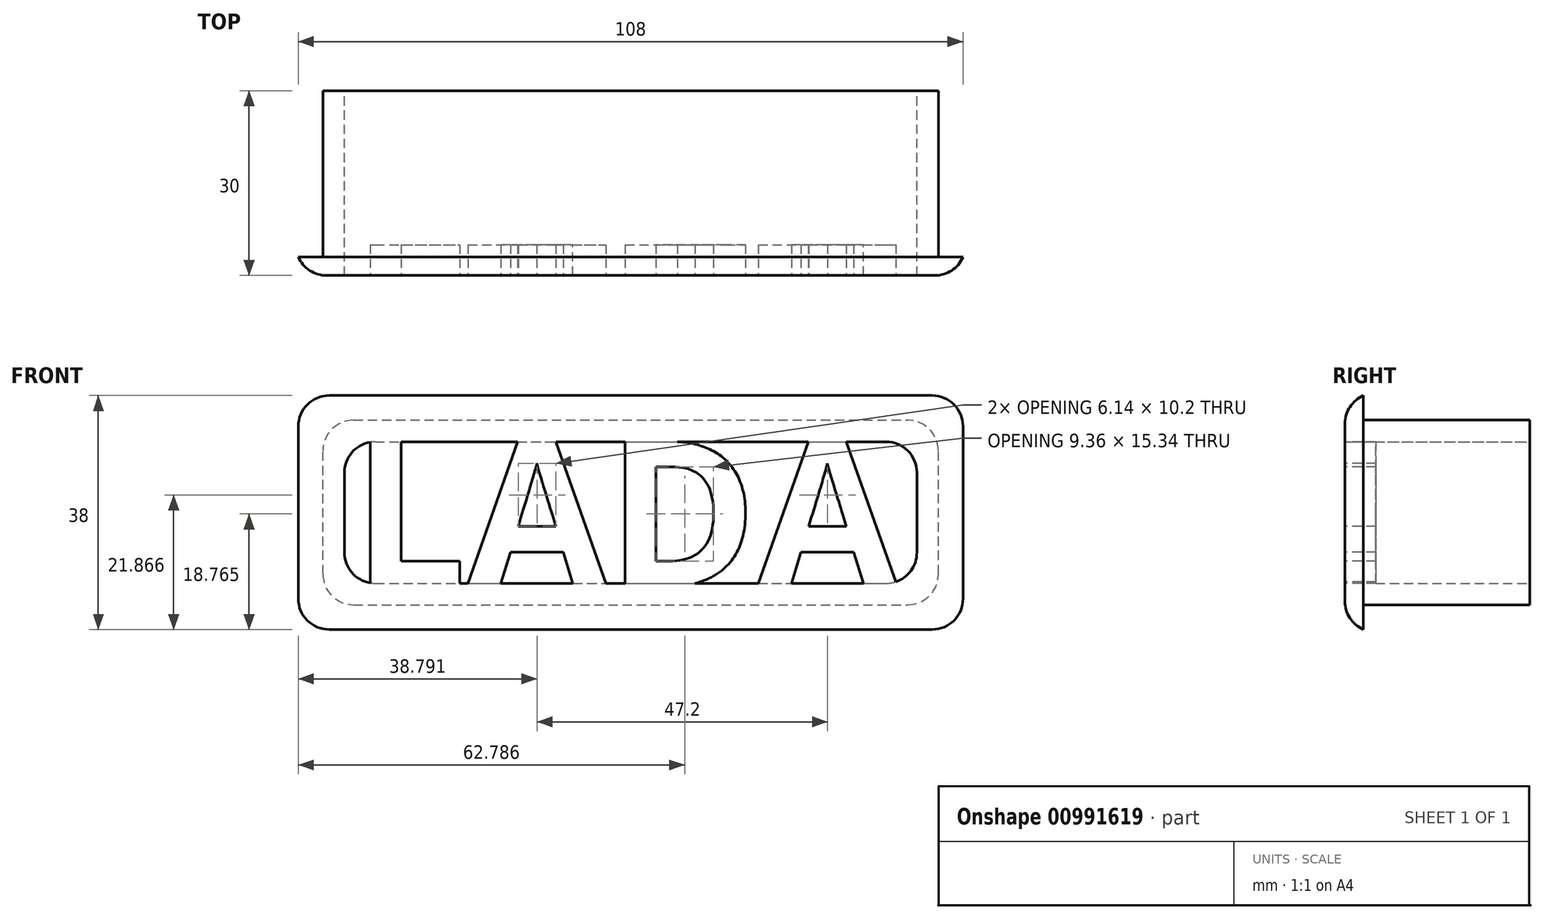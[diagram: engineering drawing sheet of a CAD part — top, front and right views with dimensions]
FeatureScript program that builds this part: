
annotation { "Feature Type Name" : "Feature", "Feature Type Description" : "" }
export const myFeature = defineFeature(function(context is Context, id is Id, definition is map)
    precondition{}
    {
        {
            var Q0;
            Q0=qCreatedBy(makeId("Front.planeOp"),FACE);
            var sketch = newSketch(context, id + "F0", { "sketchPlane" : qUnion([Q0])});
            skLineSegment(sketch, "E0.bottom", {"start": v(0, 0) * mm, "end": v(100, 0) * mm});
            skLineSegment(sketch, "E0.top", {"start": v(0, 30) * mm, "end": v(100, 30) * mm});
            skLineSegment(sketch, "E0.left", {"start": v(0, 0) * mm, "end": v(0, 30) * mm});
            skLineSegment(sketch, "E0.right", {"start": v(100, 0) * mm, "end": v(100, 30) * mm});
            skLineSegment(sketch, "E1.bottom", {"start": v(3.5, 3.5) * mm, "end": v(96.5, 3.5) * mm});
            skLineSegment(sketch, "E1.top", {"start": v(3.5, 26.5) * mm, "end": v(96.5, 26.5) * mm});
            skLineSegment(sketch, "E1.left", {"start": v(3.5, 3.5) * mm, "end": v(3.5, 26.5) * mm});
            skLineSegment(sketch, "E1.right", {"start": v(96.5, 3.5) * mm, "end": v(96.5, 26.5) * mm});
            skLineSegment(sketch, "E2", {"start": v(0, 15) * mm, "end": v(100, 15) * mm, "construction": true});
            skPoint(sketch, "E2.endSnap0", {"position": v(96.5, 15) * mm});
            skLineSegment(sketch, "E3", {"start": v(50, 30) * mm, "end": v(50, 0) * mm, "construction": true});
            skSolve(sketch);
        }
        {
            var Q0;
            Q0=makeQuery(id+"F0.imprint","IMPRINT",FACE,{"disambiguationData":[TD([[makeQuery(id+"F0.imprint","IMPRINT",EDGE,{"derivedFrom":sQuery(id+"F0.wireOp",EDGE,"E0.bottom")}),1.0]])]});
            extrude(context, id + "F1", {"entities" : qUnion([Q0]), "depth" : 30 * mm, "offsetDistance" : 25 * mm});
        }
        {
            var Q0;
            Q0=makeQuery(id+"F1.opExtrude","CAP_FACE",FACE,{"disambiguationData":[OSD([sQuery(id+"F0.wireOp",EDGE,"E0.bottom"),sQuery(id+"F0.wireOp",EDGE,"E0.top"),sQuery(id+"F0.wireOp",EDGE,"E0.left"),sQuery(id+"F0.wireOp",EDGE,"E0.right"),sQuery(id+"F0.wireOp",EDGE,"E1.bottom"),sQuery(id+"F0.wireOp",EDGE,"E1.top"),sQuery(id+"F0.wireOp",EDGE,"E1.left"),sQuery(id+"F0.wireOp",EDGE,"E1.right")])],"isStart":false});
            var sketch = newSketch(context, id + "F2", { "sketchPlane" : qUnion([Q0])});
            skLineSegment(sketch, "E4.bottom", {"start": v(1, 34) * mm, "end": v(99, 34) * mm});
            skLineSegment(sketch, "E4.top", {"start": v(1, -4) * mm, "end": v(99, -4) * mm});
            skLineSegment(sketch, "E4.left", {"start": v(-4, 29) * mm, "end": v(-4, 1) * mm});
            skLineSegment(sketch, "E4.right", {"start": v(104, 29) * mm, "end": v(104, 1) * mm});
            skPoint(sketch, "E5.visualSharp", {"position": v(-4, 34) * mm});
            skArc(sketch, "E5.filletArc", {"start": v(1, 34) * mm, "mid": v(-2.54, 32.54) * mm, "end": v(-4, 29) * mm});
            skPoint(sketch, "E6.visualSharp", {"position": v(104, 34) * mm});
            skArc(sketch, "E6.filletArc", {"start": v(104, 29) * mm, "mid": v(102.54, 32.54) * mm, "end": v(99, 34) * mm});
            skPoint(sketch, "E7.visualSharp", {"position": v(104, -4) * mm});
            skArc(sketch, "E7.filletArc", {"start": v(99, -4) * mm, "mid": v(102.54, -2.54) * mm, "end": v(104, 1) * mm});
            skPoint(sketch, "E8.visualSharp", {"position": v(-4, -4) * mm});
            skArc(sketch, "E8.filletArc", {"start": v(-4, 1) * mm, "mid": v(-2.54, -2.54) * mm, "end": v(1, -4) * mm});
            skSolve(sketch);
        }
        {
            var Q0;
            Q0=makeQuery(id+"F2.imprint","IMPRINT",FACE,{"disambiguationData":[TD([[makeQuery(id+"F2.imprint","IMPRINT",EDGE,{"derivedFrom":sQuery(id+"F2.wireOp",EDGE,"E4.bottom")}),-1.0]])]});
            extrude(context, id + "F3", {"entities" : qUnion([Q0]), "operationType" : NewBodyOperationType.ADD, "oppositeDirection" : true, "depth" : 3 * mm, "offsetDistance" : 25 * mm});
        }
        {
            var Q0;
            Q0=makeQuery(id+"F3.opExtrude","CAP_EDGE",EDGE,{"disambiguationData":[OSD([sQuery(id+"F2.wireOp",EDGE,"E6.filletArc")])],"isStart":true});
            fillet(context, id + "F4", {"entities" : qUnion([Q0]), "radius" : 5 * mm, "tangentPropagation" : true, "allowEdgeOverflow" : false});
        }
        {
            var Q0;
            Q0=makeQuery(id+"F1.opExtrude","SWEPT_EDGE",EDGE,{"disambiguationData":[OSD([sQuery(id+"F0.wireOp",EDGE,"E1.top"),sQuery(id+"F0.wireOp",EDGE,"E1.right")])]});
            var Q1;
            Q1=makeQuery(id+"F1.opExtrude","SWEPT_EDGE",EDGE,{"disambiguationData":[OSD([sQuery(id+"F0.wireOp",EDGE,"E1.bottom"),sQuery(id+"F0.wireOp",EDGE,"E1.right")])]});
            var Q2;
            Q2=makeQuery(id+"F1.opExtrude","SWEPT_EDGE",EDGE,{"disambiguationData":[OSD([sQuery(id+"F0.wireOp",EDGE,"E1.top"),sQuery(id+"F0.wireOp",EDGE,"E1.left")])]});
            var Q3;
            Q3=makeQuery(id+"F1.opExtrude","SWEPT_EDGE",EDGE,{"disambiguationData":[OSD([sQuery(id+"F0.wireOp",EDGE,"E1.bottom"),sQuery(id+"F0.wireOp",EDGE,"E1.left")])]});
            var Q4;
            Q4=makeQuery(id+"F1.opExtrude","SWEPT_EDGE",EDGE,{"disambiguationData":[OSD([sQuery(id+"F0.wireOp",EDGE,"E0.top"),sQuery(id+"F0.wireOp",EDGE,"E0.right")])]});
            var Q5;
            Q5=makeQuery(id+"F1.opExtrude","SWEPT_EDGE",EDGE,{"disambiguationData":[OSD([sQuery(id+"F0.wireOp",EDGE,"E0.top"),sQuery(id+"F0.wireOp",EDGE,"E0.left")])]});
            var Q6;
            Q6=makeQuery(id+"F1.opExtrude","SWEPT_EDGE",EDGE,{"disambiguationData":[OSD([sQuery(id+"F0.wireOp",EDGE,"E0.bottom"),sQuery(id+"F0.wireOp",EDGE,"E0.left")])]});
            var Q7;
            Q7=makeQuery(id+"F1.opExtrude","SWEPT_EDGE",EDGE,{"disambiguationData":[OSD([sQuery(id+"F0.wireOp",EDGE,"E0.bottom"),sQuery(id+"F0.wireOp",EDGE,"E0.right")])]});
            fillet(context, id + "F5", {"entities" : qUnion([Q0, Q1, Q2, Q3, Q4, Q5, Q6, Q7]), "radius" : 5 * mm, "tangentPropagation" : true, "allowEdgeOverflow" : false});
        }
        {
            var Q0;
            Q0=qCreatedBy(makeId("Front.planeOp"),FACE);
            var sketch = newSketch(context, id + "F6", { "sketchPlane" : qUnion([Q0])});
            skFitSpline(sketch, "E9", {"points": [v(-64.61, 66.28) * mm, v(-47.68, 57.17) * mm, v(-34.75, 47.89) * mm, v(-23.1, 43.7) * mm, v(-14.9, 33.87) * mm, v(-19.1, 24.22) * mm, v(-39.3, 28.4) * mm, v(-52.96, 38.42) * mm, v(-69.35, 37.87) * mm, v(-90.29, 48.07) * mm, v(-89.38, 58.45) * mm, v(-64.61, 66.28) * mm]});
            skSolve(sketch);
        }
        {
            var Q0;
            Q0=makeQuery(id+"F6.imprint","IMPRINT",FACE,{"disambiguationData":[TD([[makeQuery(id+"F6.imprint","IMPRINT",EDGE,{"derivedFrom":sQuery(id+"F6.wireOp",EDGE,"E9")}),-1.0]])]});
            extrude(context, id + "F7", {"entities" : qUnion([Q0]), "depth" : 25 * mm, "offsetDistance" : 25 * mm});
        }
        {
            var Q0;
            Q0=makeQuery(id+"F7.opExtrude","CAP_FACE",FACE,{"disambiguationData":[OSD([sQuery(id+"F6.wireOp",EDGE,"E9")])],"isStart":false});
            shell(context, id + "F8", {"entities" : qUnion([Q0]), "thickness" : 4 * mm});
        }
        {
            var Q0;
            Q0=makeQuery(id+"F7.opExtrude","SWEPT_BODY",BODY,{"disambiguationData":[OSD([sQuery(id+"F6.wireOp",EDGE,"E9")])]});
            deleteBodies(context, id + "F9", {"entities" : qUnion([Q0])});
        }
        {
            var Q0;
            {var subQ0=sQuery(id+"F0.wireOp",EDGE,"E0.right");var subQ1=sQuery(id+"F0.wireOp",EDGE,"E0.left");var subQ2=sQuery(id+"F0.wireOp",EDGE,"E0.top");var subQ3=sQuery(id+"F0.wireOp",EDGE,"E0.bottom");Q0=makeQuery(id+"F3.boolean.opBoolean","MERGE",FACE,{"derivedFrom":[makeQuery(id+"F1.opExtrude","CAP_FACE",FACE,{"disambiguationData":[OSD([subQ3,subQ2,subQ1,subQ0,sQuery(id+"F0.wireOp",EDGE,"E1.bottom"),sQuery(id+"F0.wireOp",EDGE,"E1.top"),sQuery(id+"F0.wireOp",EDGE,"E1.left"),sQuery(id+"F0.wireOp",EDGE,"E1.right")])],"isStart":false}),makeQuery(id+"F3.opExtrude","CAP_FACE",FACE,{"disambiguationData":[OSD([subQ3,subQ2,subQ1,subQ0,sQuery(id+"F2.wireOp",EDGE,"E4.bottom"),sQuery(id+"F2.wireOp",EDGE,"E4.top"),sQuery(id+"F2.wireOp",EDGE,"E4.left"),sQuery(id+"F2.wireOp",EDGE,"E4.right"),sQuery(id+"F2.wireOp",EDGE,"E5.filletArc"),sQuery(id+"F2.wireOp",EDGE,"E6.filletArc"),sQuery(id+"F2.wireOp",EDGE,"E7.filletArc"),sQuery(id+"F2.wireOp",EDGE,"E8.filletArc")])],"isStart":true})]});}
            var sketch = newSketch(context, id + "F10", { "sketchPlane" : qUnion([Q0])});
            skText(sketch, "E10", { "text": "LADA", "fontName": "OpenSans-Bold.ttf"});
            const initialGuessF10  = {"E10": [0.00473, 0.00297, 1, 0, 0.02376]};
            skSetInitialGuess(sketch, initialGuessF10);
            skSolve(sketch);
        }
        {
            var Q0;
            {var subQ0=sQuery(id+"F10.wireOp",EDGE,"E10.sketch_text.stroke-1");Q0=makeQuery(id+"F10.imprint","IMPRINT",FACE,{"disambiguationData":[TD([[makeQuery(id+"F10.imprint","IMPRINT",EDGE,{"derivedFrom":subQ0}),-1.0]])]});}
            var Q1;
            Q1=makeQuery(id+"F10.imprint","IMPRINT",FACE,{"disambiguationData":[TD([[makeQuery(id+"F10.imprint","IMPRINT",EDGE,{"derivedFrom":sQuery(id+"F10.wireOp",EDGE,"E10.sketch_text.stroke-6")}),-1.0]])]});
            var Q2;
            Q2=makeQuery(id+"F10.imprint","IMPRINT",FACE,{"disambiguationData":[TD([[makeQuery(id+"F10.imprint","IMPRINT",EDGE,{"derivedFrom":sQuery(id+"F10.wireOp",EDGE,"E10.sketch_text.stroke-18")}),-1.0]])]});
            var Q3;
            Q3=makeQuery(id+"F10.imprint","IMPRINT",FACE,{"disambiguationData":[TD([[makeQuery(id+"F10.imprint","IMPRINT",EDGE,{"derivedFrom":sQuery(id+"F10.wireOp",EDGE,"E10.sketch_text.stroke-30")}),-1.0]])]});
            var Q4;
            {var subQ0=sQuery(id+"F10.wireOp",EDGE,"E10.sketch_text.stroke-2");Q4=makeQuery(id+"F10.imprint","IMPRINT",FACE,{"disambiguationData":[TD([[makeQuery(id+"F10.imprint","IMPRINT",EDGE,{"derivedFrom":subQ0}),-1.0]])]});}
            var Q5;
            {var subQ1=sQuery(id+"F10.wireOp",EDGE,"E10.sketch_text.stroke-3");Q5=makeQuery(id+"F10.imprint","IMPRINT",FACE,{"disambiguationData":[TD([[makeQuery(id+"F10.imprint","IMPRINT",EDGE,{"derivedFrom":subQ1}),-1.0]])]});}
            var Q6;
            {var subQ7=sQuery(id+"F10.wireOp",EDGE,"E10.sketch_text.stroke-7");Q6=makeQuery(id+"F10.imprint","IMPRINT",FACE,{"disambiguationData":[TD([[makeQuery(id+"F10.imprint","IMPRINT",EDGE,{"derivedFrom":subQ7}),-1.0]])]});}
            var Q7;
            {var subQ14=sQuery(id+"F10.wireOp",EDGE,"E10.sketch_text.stroke-31");Q7=makeQuery(id+"F10.imprint","IMPRINT",FACE,{"disambiguationData":[TD([[makeQuery(id+"F10.imprint","IMPRINT",EDGE,{"derivedFrom":subQ14}),-1.0]])]});}
            extrude(context, id + "F11", {"entities" : qUnion([Q0, Q1, Q2, Q3, Q4, Q5, Q6, Q7]), "operationType" : NewBodyOperationType.ADD, "oppositeDirection" : true, "depth" : 5 * mm, "offsetDistance" : 25 * mm});
        }
        {
            var Q0;
            Q0=makeQuery(id+"F1.opExtrude","CAP_FACE",FACE,{"disambiguationData":[OSD([sQuery(id+"F0.wireOp",EDGE,"E0.bottom"),sQuery(id+"F0.wireOp",EDGE,"E0.top"),sQuery(id+"F0.wireOp",EDGE,"E0.left"),sQuery(id+"F0.wireOp",EDGE,"E0.right"),sQuery(id+"F0.wireOp",EDGE,"E1.bottom"),sQuery(id+"F0.wireOp",EDGE,"E1.top"),sQuery(id+"F0.wireOp",EDGE,"E1.left"),sQuery(id+"F0.wireOp",EDGE,"E1.right")])],"isStart":true});
            var sketch = newSketch(context, id + "F12", { "sketchPlane" : qUnion([Q0])});
            skLineSegment(sketch, "E11", {"start": v(-54.3, 46.07) * mm, "end": v(-36.88, -17.6) * mm});
            skSolve(sketch);
        }
        {
            var Q0;
            Q0=sQuery(id+"F12.wireOp",EDGE,"E11");
            extrude(context, id + "F13", {"bodyType" : ToolBodyType.SURFACE, "surfaceEntities" : qUnion([Q0]), "oppositeDirection" : true, "depth" : 50 * mm, "offsetDistance" : 25 * mm});
        }
    });
